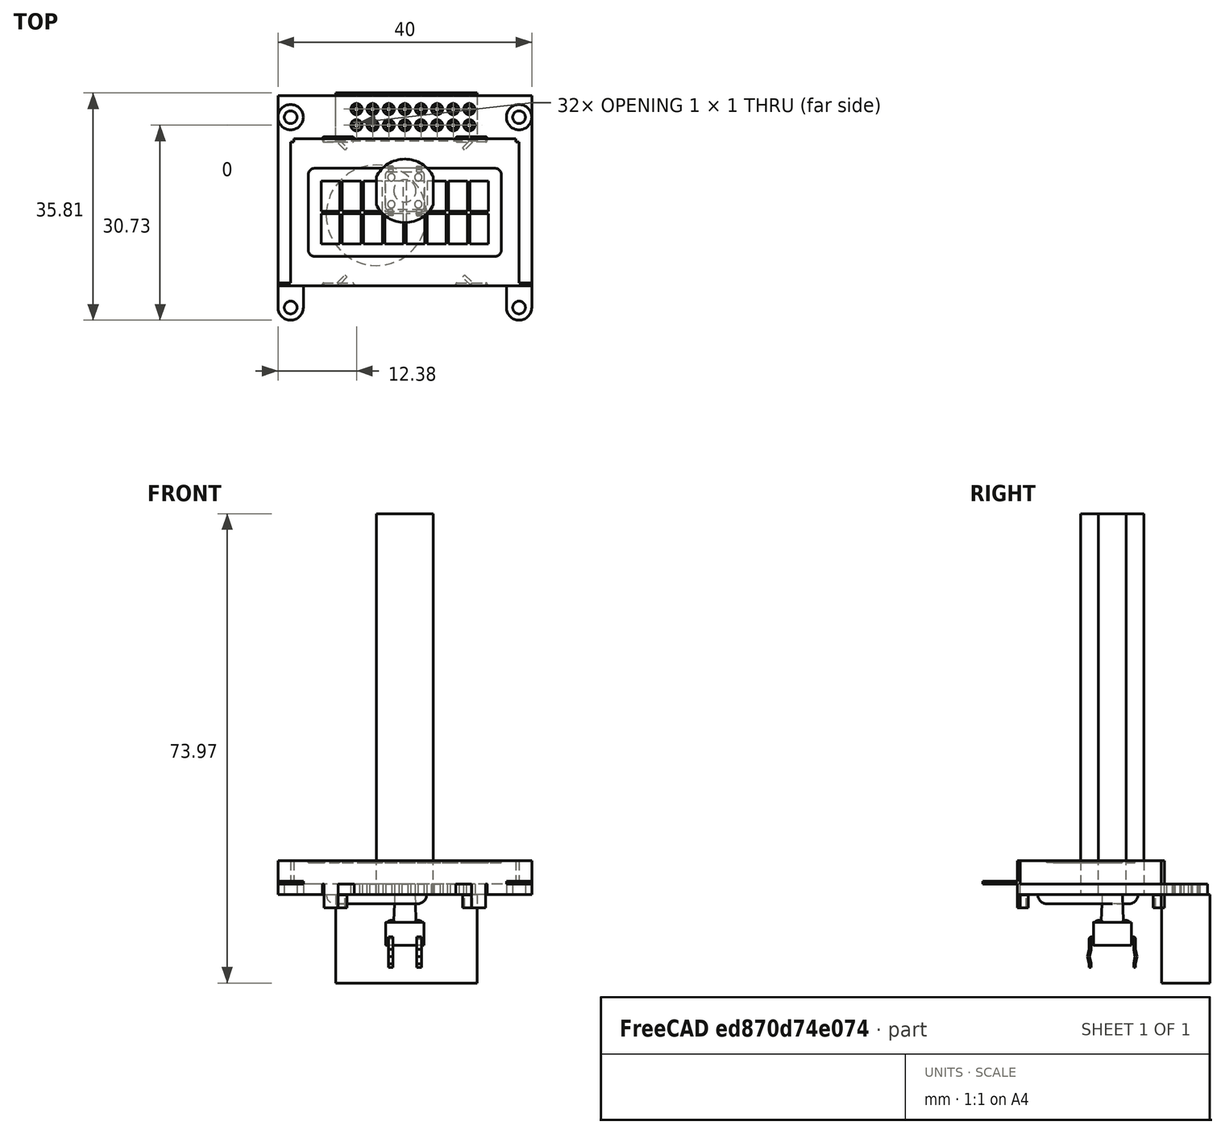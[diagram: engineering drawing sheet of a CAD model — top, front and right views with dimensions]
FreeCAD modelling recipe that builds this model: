
FCSTD DOCUMENT  (FreeCAD 1.0R39109 (Git))
Label: WwvbClockComponents
License: All rights reserved
LicenseURL: https://en.wikipedia.org/wiki/All_rights_reserved
objects: Part::Feature×20, App::Link×15, App::FeaturePython×7, Sketcher::SketchObject×2, PartDesign::Pad×2, PartDesign::SubShapeBinder×2, PartDesign::Body×2, App::Part×2, Assembly::AssemblyLink×1, Spreadsheet::Sheet×1, Assembly::JointGroup×1, Assembly::AssemblyObject×1
note: 34 computed .brp shape members not serialized (recipe doc carries the construction recipe); baked Part::Feature solids carry a one-line shape summary decoded from their .brp
EXTERNAL_REF file=ClockRaytrace.FCStd obj=Spreadsheet
EXTERNAL_REF file=ClockRaytrace.FCStd obj=Part006
EXTERNAL_REF file=PCB/PCB.FCStd obj=Assembly
EXTERNAL_REF file=PCB/PCB.FCStd obj=Teensy
EXTERNAL_REF file=PCB/PCB.FCStd obj=Part001
EXTERNAL_REF file=PCB/PCB.FCStd obj=Part003
EXTERNAL_REF file=PCB/PCB.FCStd obj=Body004
EXTERNAL_REF file=PCB/PCB.FCStd obj=Body
EXTERNAL_REF file=PCB/PCB.FCStd obj=PSK_receiver
EXTERNAL_REF file=PCB/PCB.FCStd obj=Teensy_header
EXTERNAL_REF file=PCB/PCB.FCStd obj=Teensy_header001
EXTERNAL_REF file=ClockRaytrace.FCStd obj=Body001

FEATURE [App::Link] Link002  label="Spreadsheet"
  LinkedObject = -> <external ClockRaytrace.FCStd>#Spreadsheet
FEATURE [Part::Feature] Part__Feature  label="NHD-0208AZ-RN"
  shape: bbox 4 x 4 x 1.602 mm, 6 faces (baked)
FEATURE [Part::Feature] Part__Feature001  label="NHD-0208AZ-RN001"
  shape: bbox 4 x 4 x 1.602 mm, 6 faces (baked)
FEATURE [Part::Feature] Part__Feature002  label="NHD-0208AZ-RN002"
  shape: bbox 1.8 x 1.8 x 1.602 mm, 6 faces (baked)
FEATURE [Part::Feature] Part__Feature003  label="NHD-0208AZ-RN003"
  shape: bbox 1.8 x 1.8 x 1.602 mm, 6 faces (baked)
FEATURE [Part::Feature] Part__Feature004  label="NHD-0208AZ-RN004"
  shape: bbox 1.8 x 1.8 x 1.602 mm, 6 faces (baked)
FEATURE [Part::Feature] Part__Feature005  label="NHD-0208AZ-RN005"
  shape: bbox 1.8 x 1.8 x 1.602 mm, 6 faces (baked)
FEATURE [Part::Feature] Part__Feature006  label="NHD-0208AZ-RN006"
  shape: bbox 1.8 x 1.8 x 1.602 mm, 6 faces (baked)
FEATURE [Part::Feature] Part__Feature007  label="NHD-0208AZ-RN007"
  shape: bbox 1.8 x 1.8 x 1.602 mm, 6 faces (baked)
FEATURE [Part::Feature] Part__Feature008  label="NHD-0208AZ-RN008"
  shape: bbox 1.8 x 1.8 x 1.602 mm, 6 faces (baked)
FEATURE [Part::Feature] Part__Feature009  label="NHD-0208AZ-RN009"
  shape: bbox 1.8 x 1.8 x 1.602 mm, 6 faces (baked)
FEATURE [Part::Feature] Part__Feature010  label="NHD-0208AZ-RN010"
  shape: bbox 1.8 x 1.8 x 1.602 mm, 6 faces (baked)
FEATURE [Part::Feature] Part__Feature011  label="NHD-0208AZ-RN011"
  shape: bbox 1.8 x 1.8 x 1.602 mm, 6 faces (baked)
FEATURE [Part::Feature] Part__Feature012  label="NHD-0208AZ-RN012"
  shape: bbox 1.8 x 1.8 x 1.602 mm, 6 faces (baked)
FEATURE [Part::Feature] Part__Feature013  label="NHD-0208AZ-RN013"
  shape: bbox 1.8 x 1.8 x 1.602 mm, 6 faces (baked)
FEATURE [Part::Feature] Part__Feature014  label="NHD-0208AZ-RN014"
  shape: bbox 1.8 x 1.8 x 1.602 mm, 6 faces (baked)
FEATURE [Part::Feature] Part__Feature015  label="NHD-0208AZ-RN015"
  shape: bbox 1.8 x 1.8 x 1.602 mm, 6 faces (baked)
FEATURE [Part::Feature] Part__Feature016  label="NHD-0208AZ-RN016"
  shape: bbox 1.8 x 1.8 x 1.602 mm, 6 faces (baked)
FEATURE [Part::Feature] Part__Feature017  label="NHD-0208AZ-RN017"
  shape: bbox 1.8 x 1.8 x 1.602 mm, 6 faces (baked)
FEATURE [Part::Feature] Part__Feature018  label="NHD-0208AZ-RN018"
  shape: bbox 40 x 35.4 x 7.4 mm, 222 faces (baked)
FEATURE [Part::Feature] Part__Feature019  label="Switch 1"
  shape: bbox 5.99 x 7.8 x 11.51 mm, 99 faces (baked)
FEATURE [Sketcher::SketchObject] Sketch007
  ArcFitTolerance = 1e-06
  AttachmentSupport = -> [XY_Plane016]
  FullyConstrained = true
  MakeInternals = false
  MapMode = 5
  sketch-geometry (5):
    g0: ArcOfCircle CenterX=0 CenterY=0 CenterZ=0 NormalX=0 NormalY=0 NormalZ=1 AngleXU=0 Radius=5 StartAngle=0.451027 EndAngle=2.69057
    g1: LineSegment StartX=4.5 StartY=-2.17945 StartZ=0 EndX=4.5 EndY=2.17945 EndZ=0
    g2: LineSegment StartX=-4.5 StartY=2.17945 StartZ=0 EndX=-4.5 EndY=-2.17945 EndZ=0
    g3: GeomPoint [constr] X=0 Y=0 Z=0
    g4: ArcOfCircle CenterX=0 CenterY=0 CenterZ=0 NormalX=0 NormalY=0 NormalZ=1 AngleXU=0 Radius=5 StartAngle=3.59262 EndAngle=5.83216
  constraints (14):
    c: Coincident(g0,g-1)
    c: Diameter(g0) = 10
    c: Vertical(g1)
    c: Vertical(g2)
    c: Coincident(g3,g0)
    c: Coincident(g0,g1)
    c: Coincident(g1,g4)
    c: PointOnObject(g2,g4)
    c: Equal(g0,g4)
    c: PointOnObject(g4,g2)
    c: Coincident(g0,g4)
    c: Coincident(g2,g0)
    c: DistanceX(g0,g0) = 9
    c: Equal(g2,g1)
FEATURE [PartDesign::Pad] Pad005
  Direction = (0,0,1)
  Length = 60
  Length2 = 10
  Profile = -> Sketch007
  ReferenceAxis = -> Sketch007 [N_Axis]
  Refine = true
  Suppressed = false
  Type = 0
FEATURE [App::Link] LED
  LinkPlacement = pos=(15,0,-5.08) rot=(0,0,1;1.5708rad)
  LinkedObject = -> <external ClockRaytrace.FCStd>#Part006
  Placement = pos=(15,0,-5.08) rot=(0,0,1;1.5708rad)
  expr: .Placement.Base.z = -<<Spreadsheet>>.Base_LED_Package_Height
  expr: .Placement.Rotation.Yaw = <<Spreadsheet>>.Base_LED_yaw_angle
FEATURE [App::FeaturePython] GroundedJoint  label="LED002"  # Assembly grounded joint (typed FeaturePython)
  ObjectToGround = -> LED
  Placement = pos=(15,0,-5.08) rot=(0,0,1;1.5708rad)
FEATURE [App::Link] Teensy  label="Teensy001"
  LinkPlacement = pos=(22.0851,8.84038,14.921) rot=(0,0,1;4.71239rad)
  LinkedObject = -> <external PCB/PCB.FCStd>#Teensy
  Placement = pos=(22.0851,8.84038,14.921) rot=(0,0,1;4.71239rad)
FEATURE [App::Link] Part001  label="PJ-202A"
  LinkPlacement = pos=(35.1848,67.2072,8.325) rot=(0.57735,0.57735,0.57735;2.0944rad)
  LinkedObject = -> <external PCB/PCB.FCStd>#Part001
  Placement = pos=(35.1848,67.2072,8.325) rot=(0.57735,0.57735,0.57735;2.0944rad)
FEATURE [App::Link] Part003  label="connect to LCD"
  LinkPlacement = pos=(38.0997,17.4048,-0.214) rot=(0.57735,0.57735,-0.57735;4.18879rad)
  LinkedObject = -> <external PCB/PCB.FCStd>#Part003
  Placement = pos=(38.0997,17.4048,-0.214) rot=(0.57735,0.57735,-0.57735;4.18879rad)
FEATURE [App::Link] Body004  label="PCB"
  LinkedObject = -> <external PCB/PCB.FCStd>#Body004
FEATURE [App::Link] LED001
  LinkPlacement = pos=(25.16,1.4e-15,-5.08) rot=(0,0,1;1.5708rad)
  LinkedObject = -> <external ClockRaytrace.FCStd>#Part006
  Placement = pos=(25.16,1.4e-15,-5.08) rot=(0,0,1;1.5708rad)
FEATURE [App::FeaturePython] Joint001  label="Fixed"  # Assembly joint (typed FeaturePython)
  Activated = true
  AngleMax = 0
  AngleMin = 0
  Detach1 = false
  Detach2 = false
  Distance = 0
  Distance2 = 0
  EnableAngleMax = false
  EnableAngleMin = false
  EnableLengthMax = false
  EnableLengthMin = false
  JointType = 0 (Fixed)
  LengthMax = 0
  LengthMin = 0
  Offset1 = pos=(0,0,0) rot=(0,0,1;3.14159rad)
  Placement1 = pos=(2e-16,5.08,2.54) rot=(0,0.707107,0.707107;3.14159rad)
  Placement2 = pos=(-2e-16,-5.08,2.54) rot=(0,-0.707107,0.707107;3.14159rad)
  Reference1 = -> Assembly [LED001.Body.Face2,LED001.Body.Face2]
  Reference2 = -> Assembly [LED.Body.Face3,LED.Body.Face3]
FEATURE [App::FeaturePython] GroundedJoint002  label="2nd LED"  # Assembly grounded joint (typed FeaturePython)
  ObjectToGround = -> LED001
  Placement = pos=(25.16,1.4e-15,-5.08) rot=(0,0,1;1.5708rad)
FEATURE [App::Link] Body008  label="Keystone 103"
  LinkPlacement = pos=(26.67,34.635,-2.52) rot=(0.707107,0.707107,0;3.14159rad)
  LinkedObject = -> <external PCB/PCB.FCStd>#Body
  Placement = pos=(26.67,34.635,-2.52) rot=(0.707107,0.707107,0;3.14159rad)
FEATURE [App::Link] PSK_receiver  label="PSK receiver"
  LinkPlacement = pos=(-36.1561,29.1871,-3.151) rot=(0,0,1;0rad)
  LinkedObject = -> <external PCB/PCB.FCStd>#PSK_receiver
  Placement = pos=(-36.1561,29.1871,-3.151) rot=(0,0,1;0rad)
FEATURE [App::FeaturePython] Joint  label="Revolute"  # Assembly joint (typed FeaturePython)
  Activated = true
  AngleMax = 0
  AngleMin = 0
  Detach1 = false
  Detach2 = false
  Distance = 0
  Distance2 = 0
  EnableAngleMax = false
  EnableAngleMin = false
  EnableLengthMax = false
  EnableLengthMin = false
  JointType = 1 (Revolute)
  LengthMax = 0
  LengthMin = 0
  Offset1 = pos=(0,0,-2.413) rot=(0,0,1;3.14159rad)
  Placement1 = pos=(-6.35,-3.81,-1.905) rot=(0,-1,0;3.14159rad)
  Placement2 = pos=(23.6297,62.23,0) rot=(0,0,1;0rad)
  Reference1 = -> Assembly [LED001.Body.Edge18,LED001.Body.Edge18]
  Reference2 = -> Assembly [Assembly001.Body004.HoleSketch.Edge10,Assembly001.Body004.HoleSketch.Edge10]
FEATURE [PartDesign::SubShapeBinder] Binder
  BindCopyOnChange = 0
  BindMode = 0
  ClaimChildren = false
  Context = -> Part [Body007.Binder.]
  Fuse = false
  MakeFace = true
  OffsetFill = false
  OffsetIntersection = false
  OffsetJoinType = 0
  OffsetOpenResult = false
  PartialLoad = false
  Refine = true
  Relative = true
  Support = -> [Assembly[Assembly001.Body008.Pad001.Face1]]
  _Version = 2
FEATURE [PartDesign::Body] Body007
  AllowCompound = false
  Group = -> [Sketch007,Pad005,Binder]
  Origin = -> Origin016
  Tip = -> Pad005
FEATURE [App::Part] Part  label="Antenna"
  Group = -> [Body007]
  Origin = -> Origin015
  Placement = pos=(-31.75,-2.54,-22.86) rot=(0.57735,0.57735,0.57735;2.0944rad)
FEATURE [App::Link] LCD_panel  label="LCD panel001"
  LinkPlacement = pos=(-29.21,-3.556,33.02) rot=(0.497543,-0.497543,-0.710565;1.90603rad)
  LinkedObject = -> NHD_0208AZ_RN
  Placement = pos=(-29.21,-3.556,33.02) rot=(0.497543,-0.497543,-0.710565;1.90603rad)
FEATURE [App::Link] Teensy_header  label="Teensy header"
  LinkPlacement = pos=(62.8687,-3.88149,1.778) rot=(0,0,1;1.5708rad)
  LinkedObject = -> <external PCB/PCB.FCStd>#Teensy_header
  Placement = pos=(62.8687,-3.88149,1.778) rot=(0,0,1;1.5708rad)
FEATURE [App::Link] Teensy_header001  label="Teensy header001"
  LinkPlacement = pos=(62.8687,11.3585,1.778) rot=(0,0,1;1.5708rad)
  LinkedObject = -> <external PCB/PCB.FCStd>#Teensy_header001
  Placement = pos=(62.8687,11.3585,1.778) rot=(0,0,1;1.5708rad)
FEATURE [Assembly::AssemblyLink] Assembly001  label="PCB001"
  Group = -> [Teensy,Part001,Part003,Body004,Body008,PSK_receiver,Teensy_header,Teensy_header001]
  LinkedObject = -> <external PCB/PCB.FCStd>#Assembly
  Origin = -> Origin018
  Placement = pos=(-33.26,17.2797,-6.985) rot=(0,0,-1;1.5708rad)
  Rigid = true
FEATURE [App::FeaturePython] GroundedJoint003  label="LCD"  # Assembly grounded joint (typed FeaturePython)
  ObjectToGround = -> LCD_panel
  Placement = pos=(-29.21,-3.556,33.02) rot=(0.497543,-0.497543,-0.710565;1.90603rad)
FEATURE [App::Link] _8mm50FLLens  label="38mm50FLLens"
  LinkPlacement = pos=(5,0,51) rot=(0,0,1;0rad)
  LinkedObject = -> <external ClockRaytrace.FCStd>#Body001
  Placement = pos=(5,0,51) rot=(0,0,1;0rad)
  expr: .Placement.Base.x = 15 mm - <<Spreadsheet>>.Base_Lens_X_offset
  expr: .Placement.Base.z = <<Spreadsheet>>.Base_LensToLED
FEATURE [PartDesign::SubShapeBinder] Binder001
  BindCopyOnChange = 0
  BindMode = 0
  ClaimChildren = false
  Context = -> NHD_0208AZ_RN [Body.Binder001.]
  Fuse = false
  MakeFace = true
  OffsetFill = false
  OffsetIntersection = false
  OffsetJoinType = 0
  OffsetOpenResult = false
  PartialLoad = false
  Refine = true
  Relative = true
  Support = -> [Part__Feature018]
  _Version = 2
FEATURE [Sketcher::SketchObject] Sketch
  ArcFitTolerance = 1e-06
  AttachmentSupport = -> [Binder001]
  ExternalGeometry = -> [Binder001]
  FullyConstrained = true
  MakeInternals = false
  MapMode = 5
  Placement = pos=(0,0,0) rot=(1,0,0;3.14159rad)
  sketch-geometry (4):
    g0: LineSegment StartX=-10.922 StartY=-7.79 StartZ=0 EndX=-10.922 EndY=-15.41 EndZ=0
    g1: LineSegment StartX=-10.922 StartY=-15.41 StartZ=0 EndX=11.422 EndY=-15.41 EndZ=0
    g2: LineSegment StartX=11.422 StartY=-15.41 StartZ=0 EndX=11.422 EndY=-7.79 EndZ=0
    g3: LineSegment StartX=11.422 StartY=-7.79 StartZ=0 EndX=-10.922 EndY=-7.79 EndZ=0
  constraints (12):
    c: Coincident(g0,g1)
    c: Coincident(g1,g2)
    c: Coincident(g2,g3)
    c: Coincident(g3,g0)
    c: Vertical(g0)
    c: Vertical(g2)
    c: Horizontal(g1)
    c: Horizontal(g3)
    c: DistanceX(g0,g-4) = 3.302
    c: DistanceX(g-3,g2) = 3.302
    c: DistanceY(g0,g-4) = 2.54
    c: DistanceY(g-3,g2) = 2.54
FEATURE [PartDesign::Pad] Pad
  Direction = (0,0,-1)
  Length = 13.97
  Length2 = 10
  Profile = -> Sketch
  ReferenceAxis = -> Sketch [N_Axis]
  Refine = true
  Suppressed = false
  Type = 0
FEATURE [PartDesign::Body] Body
  AllowCompound = false
  Group = -> [Binder001,Sketch,Pad]
  Origin = -> Origin019
  Tip = -> Pad
FEATURE [App::Part] NHD_0208AZ_RN  label="LCD panel"
  Group = -> [Part__Feature,Part__Feature001,Part__Feature002,Part__Feature003,Part__Feature004,Part__Feature005,Part__Feature006,Part__Feature007,Part__Feature008,Part__Feature009,Part__Feature010,Part__Feature011,Part__Feature012,Part__Feature013,Part__Feature014,Part__Feature015,Part__Feature016,Part__Feature017,Part__Feature018,Body]
  Origin = -> Origin
FEATURE [App::Link] Switch_1  label="Switch 002"
  LinkPlacement = pos=(-17.5,-20,53.3) rot=(0,0,1;0rad)
  LinkedObject = -> Part__Feature019
  Placement = pos=(-17.5,-20,53.3) rot=(0,0,1;0rad)
FEATURE [App::Link] Switch_002  label="Switch 003"
  LinkPlacement = pos=(-17.5,13.61,53.3) rot=(0,0,1;0rad)
  LinkedObject = -> Part__Feature019
  Placement = pos=(-17.5,13.61,53.3) rot=(0,0,1;0rad)
FEATURE [Spreadsheet::Sheet] Spreadsheet  label="Spreadsheet001"
  Base_Antenna_X_Offset = 0
  Base_Antenna_Y_Offset = 2.54
  Base_Antenna_Z_Offset = -25.4
FEATURE [App::FeaturePython] GroundedJoint005  # Assembly grounded joint (typed FeaturePython)
  ObjectToGround = -> Switch_002
  Placement = pos=(-17.5,13.61,53.3) rot=(0,0,1;0rad)
FEATURE [App::FeaturePython] GroundedJoint006  # Assembly grounded joint (typed FeaturePython)
  ObjectToGround = -> Switch_1
  Placement = pos=(-17.5,-20,53.3) rot=(0,0,1;0rad)
FEATURE [Assembly::JointGroup] Joints
  Group = -> [GroundedJoint,Joint001,GroundedJoint002,Joint,GroundedJoint003,GroundedJoint005,GroundedJoint006]
FEATURE [Assembly::AssemblyObject] Assembly
  Group = -> [Joints,LED,GroundedJoint,Assembly001,LED001,Joint001,GroundedJoint002,Joint,LCD_panel,GroundedJoint003,_8mm50FLLens,Switch_1,Switch_002,GroundedJoint005,GroundedJoint006]
  Origin = -> Origin017
  Type = Assembly

RESOLVED EXTERNAL PARTS (link-assembly join: the EXTERNAL_REF files above that resolve inside this repo's crawl, each included once):
---- part ClockRaytrace.FCStd = doc fcstd_c784e775d372 ----
FCSTD DOCUMENT  (FreeCAD 1.0R39109 (Git))
Label: ClockRaytrace
License: All rights reserved
LicenseURL: https://en.wikipedia.org/wiki/All_rights_reserved
objects: Part::FeaturePython×11, Sketcher::SketchObject×5, PartDesign::Body×4, PartDesign::Pad×4, App::Link×2, App::DocumentObjectGroup×2, PartDesign::Revolution×1, PartDesign::ShapeBinder×1, Spreadsheet::Sheet×1, App::Part×1
note: 41 computed .brp shape members not serialized (recipe doc carries the construction recipe); baked Part::Feature solids carry a one-line shape summary decoded from their .brp

FEATURE [Sketcher::SketchObject] Sketch001
  ArcFitTolerance = 1e-06
  AttachmentSupport = -> [XZ_Plane003]
  FullyConstrained = true
  MakeInternals = false
  MapMode = 5
  Placement = pos=(0,0,0) rot=(1,0,0;1.5708rad)
  sketch-geometry (7):
    g0: LineSegment StartX=0 StartY=3.99545 StartZ=0 EndX=0 EndY=-3.99545 EndZ=0
    g1: LineSegment [constr] StartX=0 StartY=0 StartZ=0 EndX=19 EndY=0 EndZ=0
    g2: LineSegment StartX=19 StartY=0.4 StartZ=0 EndX=19 EndY=-0.4 EndZ=0
    g3: Circle [constr] CenterX=0 CenterY=-48.0045 CenterZ=0 NormalX=0 NormalY=0 NormalZ=1 AngleXU=0 Radius=52
    g4: ArcOfCircle CenterX=1.31e-14 CenterY=-48.0045 CenterZ=0 NormalX=0 NormalY=0 NormalZ=1 AngleXU=0 Radius=52 StartAngle=1.19675 EndAngle=1.5708
    g5: Circle [constr] CenterX=0 CenterY=48.0045 CenterZ=0 NormalX=0 NormalY=0 NormalZ=1 AngleXU=0 Radius=52
    g6: ArcOfCircle CenterX=4.1e-15 CenterY=48.0045 CenterZ=0 NormalX=0 NormalY=0 NormalZ=1 AngleXU=0 Radius=52 StartAngle=4.71239 EndAngle=5.08643
  constraints (21):
    c: Vertical(g0)
    c: Symmetric(g0,g0,g-1)
    c: Coincident(g1,g-1)
    c: PointOnObject(g1,g-1)
    c: DistanceX(g1,g1) = 19
    c: Vertical(g2)
    c: Symmetric(g2,g2,g1)
    c: Radius(g3) = 52
    c: Vertical(g3,g0)
    c: PointOnObject(g2,g3)
    c: PointOnObject(g0,g3)
    c: Coincident(g4,g0)
    c: Coincident(g4,g2)
    c: Vertical(g5,g0)
    c: Equal(g5,g3)
    c: PointOnObject(g2,g5)
    c: Coincident(g6,g2)
    c: Coincident(g6,g0)
    c: Equal(g4,g3)
    c: Equal(g5,g6)
    c: DistanceY(g2,g2) = 0.8
FEATURE [PartDesign::Revolution] Revolution001
  Angle = 360
  Angle2 = 60
  Axis = (0,2e-16,1)
  Base = (0,0,0)
  Placement = pos=(0,0,0) rot=(1,0,0;1.5708rad)
  Profile = -> Sketch001
  ReferenceAxis = -> Sketch001 [V_Axis]
  Refine = true
  Reversed = true
  Suppressed = false
  Type = 0
FEATURE [PartDesign::Body] Body001  label="38mm50FLLens"
  AllowCompound = false
  Group = -> [Sketch001,Revolution001]
  Origin = -> Origin003
  Tip = -> Revolution001
FEATURE [Part::FeaturePython] Beam  # WARN: FeaturePython — macro-defined, semantics opaque (R4)
  BeamDistance = 0.1
  BeamNrColumns = 10
  BeamNrRows = 10
  ConeAngle = 90
  HideFirstPart = false
  MaxNrReflections = 200
  MaxRayLength = 1000000
  Order = 0
  Placement = pos=(1.855,-7.73,0) rot=(-1,0,0;0.05236rad)
  Power = true
  Spherical = true
  Wavelength = 580
  expr: .Placement.Base.x = Spreadsheet.Base_LED_Height / 2 + Spreadsheet.Base_LED_X_offset
  expr: .Placement.Base.y = -Spreadsheet.Base_LED_Width / 2
  expr: BeamNrColumns = Spreadsheet.Base_Source_Columns
  expr: BeamNrRows = Spreadsheet.Base_Source_Rows
  expr: ConeAngle = Spreadsheet.Base_SourceConeAngle
FEATURE [Part::FeaturePython] Beam001  # WARN: FeaturePython — macro-defined, semantics opaque (R4)
  BeamDistance = 0.1
  BeamNrColumns = 10
  BeamNrRows = 10
  ConeAngle = 90
  HideFirstPart = false
  MaxNrReflections = 200
  MaxRayLength = 1000000
  Order = 0
  Placement = pos=(-1.855,0,0) rot=(0,1,0;0rad)
  Power = true
  Spherical = true
  Wavelength = 580
  expr: .Placement.Base.x = -Spreadsheet.Base_LED_Height / 2 + Spreadsheet.Base_LED_X_offset
  expr: BeamNrColumns = Spreadsheet.Base_Source_Columns
  expr: BeamNrRows = Spreadsheet.Base_Source_Rows
  expr: ConeAngle = Spreadsheet.Base_SourceConeAngle
FEATURE [Part::FeaturePython] Beam002  # WARN: FeaturePython — macro-defined, semantics opaque (R4)
  BeamDistance = 1
  BeamNrColumns = 40
  BeamNrRows = 1
  ConeAngle = 360
  HideFirstPart = false
  MaxNrReflections = 200
  MaxRayLength = 1000000
  Order = 0
  Placement = pos=(20,0,0) rot=(0.57735,-0.57735,0.57735;2.0944rad)
  Power = true
  Spherical = false
  Wavelength = 580
FEATURE [Part::FeaturePython] Beam003  # WARN: FeaturePython — macro-defined, semantics opaque (R4)
  BeamDistance = 0.1
  BeamNrColumns = 10
  BeamNrRows = 10
  ConeAngle = 90
  HideFirstPart = false
  MaxNrReflections = 200
  MaxRayLength = 1000000
  Order = 0
  Placement = pos=(1.855,7.73,0) rot=(1,0,0;0.069813rad)
  Power = true
  Spherical = true
  Wavelength = 580
  expr: .Placement.Base.x = Spreadsheet.Base_LED_Height / 2 + Spreadsheet.Base_LED_X_offset
  expr: .Placement.Base.y = Spreadsheet.Base_LED_Width / 2
  expr: BeamNrColumns = Spreadsheet.Base_Source_Columns
  expr: BeamNrRows = Spreadsheet.Base_Source_Rows
  expr: ConeAngle = Spreadsheet.Base_SourceConeAngle
FEATURE [PartDesign::ShapeBinder] CopyPad004
  TraceSupport = false
FEATURE [Sketcher::SketchObject] Sketch
  ArcFitTolerance = 1e-06
  AttachmentSupport = -> [CopyPad004]
  FullyConstrained = true
  MakeInternals = false
  MapMode = 5
  Placement = pos=(0,0,0) rot=(1,0,0;3.14159rad)
  sketch-geometry (5):
    g0: LineSegment StartX=8.89 StartY=-5.08 StartZ=0 EndX=8.89 EndY=5.08 EndZ=0
    g1: LineSegment StartX=8.89 StartY=5.08 StartZ=0 EndX=-8.89 EndY=5.08 EndZ=0
    g2: LineSegment StartX=-8.89 StartY=5.08 StartZ=0 EndX=-8.89 EndY=-5.08 EndZ=0
    g3: LineSegment StartX=-8.89 StartY=-5.08 StartZ=0 EndX=8.89 EndY=-5.08 EndZ=0
    g4: GeomPoint [constr] X=0 Y=0 Z=0
  constraints (12):
    c: Coincident(g0,g1)
    c: Coincident(g1,g2)
    c: Coincident(g2,g3)
    c: Coincident(g3,g0)
    c: Vertical(g0)
    c: Vertical(g2)
    c: Horizontal(g1)
    c: Horizontal(g3)
    c: Symmetric(g2,g0,g4)
    c: Coincident(g4,g-1)
    c: DistanceY(g0,g0) = 10.16
    c: DistanceX(g1,g1) = 17.78
FEATURE [PartDesign::Pad] Pad
  Direction = (0,0,-1)
  Length = 5.08
  Length2 = 10
  Profile = -> Sketch
  ReferenceAxis = -> Sketch [N_Axis]
  Refine = true
  Reversed = true
  Suppressed = false
  Type = 0
FEATURE [Sketcher::SketchObject] Sketch011
  ArcFitTolerance = 1e-06
  AttachmentSupport = -> [XY_Plane019]
  FullyConstrained = false
  MakeInternals = false
  MapMode = 5
  sketch-geometry (3):
    g0: Circle CenterX=0 CenterY=0 CenterZ=0 NormalX=0 NormalY=0 NormalZ=1 AngleXU=0 Radius=20
    g1: Circle CenterX=0 CenterY=0 CenterZ=0 NormalX=0 NormalY=0 NormalZ=1 AngleXU=0 Radius=21.5748
    g2: LineSegment [constr] StartX=0.010426 StartY=20 StartZ=0 EndX=0.010426 EndY=21.5748 EndZ=0
  constraints (7):
    c: Coincident(g0,g-1)
    c: Coincident(g1,g0)
    c: Diameter(g0) = 40
    c: PointOnObject(g2,g0)
    c: PointOnObject(g2,g1)
    c: Vertical(g2)
    c: DistanceY(g2,g2) = 1.5748
FEATURE [PartDesign::Pad] Pad006
  Direction = (0,0,1)
  Length = 48
  Length2 = 10
  Profile = -> Sketch011
  ReferenceAxis = -> Sketch011 [N_Axis]
  Refine = true
  Reversed = true
  Suppressed = false
  Type = 0
  expr: Length = Spreadsheet.Base_LensToLED - 3 mm
FEATURE [PartDesign::Body] Body010  label="baffle"
  AllowCompound = false
  Group = -> [Sketch011,Pad006]
  Origin = -> Origin019
  Placement = pos=(-7.46,0,48) rot=(0,-1,0;0.314159rad)
  Tip = -> Pad006
  expr: .Placement.Base.x = 2.54 mm - Spreadsheet.Base_Lens_X_offset
  expr: .Placement.Base.z = Spreadsheet.Base_LensToLED - 3 mm
FEATURE [Part::FeaturePython] Absorber001  # WARN: FeaturePython — macro-defined, semantics opaque (R4)
  Base = -> [Body010]
  OpticalType = 1
  Transparency = 0
  collectStatistics = false
FEATURE [Spreadsheet::Sheet] Spreadsheet
  Base_Ceiling_Target_Height = 101.6
  Base_Ceiling_Target_Width = 254
  Base_DeviceTilt = 0
  Base_LED_Height = 3.71
  Base_LED_Package_Height = 5.08
  Base_LED_Width = 15.46
  Base_LED_X_offset = 0
  Base_LED_Y_offset = 0
  Base_LED_yaw_angle = 90
  Base_LEDtoCeiling = 1397
  Base_LensToLED = 51
  Base_Lens_X_offset = 10
  Base_SourceConeAngle = 90
  Base_Source_Columns = 10
  Base_Source_Rows = 10
  Base_XOffset_LED_to_Ceiling = -248.158
FEATURE [Part::FeaturePython] Beam004  # WARN: FeaturePython — macro-defined, semantics opaque (R4)
  BeamDistance = 0.1
  BeamNrColumns = 10
  BeamNrRows = 10
  ConeAngle = 90
  HideFirstPart = false
  MaxNrReflections = 200
  MaxRayLength = 1000000
  Order = 0
  Placement = pos=(-1.855,-7.73,0) rot=(-1,0,0;0.05236rad)
  Power = true
  Spherical = true
  Wavelength = 580
  expr: .Placement.Base.x = -Spreadsheet.Base_LED_Height / 2 + Spreadsheet.Base_LED_X_offset
  expr: .Placement.Base.y = -Spreadsheet.Base_LED_Width / 2
  expr: BeamNrColumns = Spreadsheet.Base_Source_Columns
  expr: BeamNrRows = Spreadsheet.Base_Source_Rows
  expr: ConeAngle = Spreadsheet.Base_SourceConeAngle
FEATURE [Part::FeaturePython] Beam005  # WARN: FeaturePython — macro-defined, semantics opaque (R4)
  BeamDistance = 0.1
  BeamNrColumns = 10
  BeamNrRows = 10
  ConeAngle = 90
  HideFirstPart = false
  MaxNrReflections = 200
  MaxRayLength = 1000000
  Order = 0
  Placement = pos=(1.855,0,0) rot=(-1,0,0;0.05236rad)
  Power = true
  Spherical = true
  Wavelength = 580
  expr: .Placement.Base.x = Spreadsheet.Base_LED_Height / 2 + <<Spreadsheet>>.Base_LED_X_offset
  expr: .Placement.Base.y = 0 in
  expr: BeamNrColumns = Spreadsheet.Base_Source_Columns
  expr: BeamNrRows = Spreadsheet.Base_Source_Rows
  expr: ConeAngle = Spreadsheet.Base_SourceConeAngle
FEATURE [Part::FeaturePython] Beam006  # WARN: FeaturePython — macro-defined, semantics opaque (R4)
  BeamDistance = 0.1
  BeamNrColumns = 10
  BeamNrRows = 10
  ConeAngle = 90
  HideFirstPart = false
  MaxNrReflections = 200
  MaxRayLength = 1000000
  Order = 0
  Placement = pos=(-1.855,7.73,0) rot=(1,0,0;0.069813rad)
  Power = true
  Spherical = true
  Wavelength = 580
  expr: .Placement.Base.x = -Spreadsheet.Base_LED_Height / 2 + Spreadsheet.Base_LED_X_offset
  expr: .Placement.Base.y = Spreadsheet.Base_LED_Width / 2
  expr: BeamNrColumns = Spreadsheet.Base_Source_Columns
  expr: BeamNrRows = Spreadsheet.Base_Source_Rows
  expr: ConeAngle = Spreadsheet.Base_SourceConeAngle
FEATURE [Sketcher::SketchObject] Sketch012
  ArcFitTolerance = 1e-06
  AttachmentSupport = -> [XZ_Plane022]
  FullyConstrained = true
  MakeInternals = false
  MapMode = 5
  Placement = pos=(0,0,0) rot=(0,0.707107,0.707107;3.14159rad)
  sketch-geometry (6):
    g0: LineSegment StartX=-76.2 StartY=0 StartZ=0 EndX=-76.2 EndY=1390.42 EndZ=0
    g1: LineSegment StartX=-76.2 StartY=1390.42 StartZ=0 EndX=1751.03 EndY=1390.42 EndZ=0
    g2: LineSegment StartX=1751.03 StartY=1390.42 StartZ=0 EndX=1751.03 EndY=1391.99 EndZ=0
    g3: LineSegment StartX=1751.03 StartY=1391.99 StartZ=0 EndX=-77.7748 EndY=1391.99 EndZ=0
    g4: LineSegment StartX=-77.7748 StartY=1391.99 StartZ=0 EndX=-77.7748 EndY=0 EndZ=0
    g5: LineSegment StartX=-77.7748 StartY=0 StartZ=0 EndX=-76.2 EndY=0 EndZ=0
  constraints (18):
    c: Vertical(g0)
    c: Horizontal(g1)
    c: Coincident(g2,g1)
    c: Vertical(g2)
    c: Horizontal(g3)
    c: PointOnObject(g4,g-1)
    c: Vertical(g4)
    c: Coincident(g5,g0)
    c: DistanceY(g2,g2) = 1.5748
    c: Equal(g5,g2)
    c: Coincident(g3,g2)
    c: Coincident(g3,g4)
    c: Coincident(g1,g0)
    c: Coincident(g5,g4)
    c: DistanceX(g0,g-1) = 76.2
    c: DistanceY(g4,g4) = 1391.99
    c: DistanceX(g3,g3) = 1828.8
    c: Horizontal(g0,g-1)
FEATURE [PartDesign::Pad] Pad007
  Direction = (0,1,-2e-16)
  Length = 1524
  Length2 = 10
  Midplane = true
  Placement = pos=(0,0,0) rot=(1,0,0;1.5708rad)
  Profile = -> Sketch012
  ReferenceAxis = -> Sketch012 [N_Axis]
  Refine = true
  Suppressed = false
  Type = 0
FEATURE [PartDesign::Body] Body011  label="Wall and Ceiling"
  AllowCompound = false
  Group = -> [Sketch012,Pad007]
  Origin = -> Origin020
  Tip = -> Pad007
  expr: .Placement.Rotation.Pitch = Spreadsheet.Base_DeviceTilt
FEATURE [Part::FeaturePython] Absorber  # WARN: FeaturePython — macro-defined, semantics opaque (R4)
  Base = -> [Body011]
  OpticalType = 1
  Transparency = 0
  collectStatistics = false
FEATURE [Sketcher::SketchObject] Sketch013
  ArcFitTolerance = 1e-06
  AttachmentSupport = -> [CopyPad004]
  FullyConstrained = true
  MakeInternals = false
  MapMode = 5
  Placement = pos=(0,0,0) rot=(1,0,0;3.14159rad)
  sketch-geometry (9):
    g0: LineSegment [constr] StartX=6.35 StartY=-3.81 StartZ=0 EndX=6.35 EndY=3.81 EndZ=0
    g1: LineSegment [constr] StartX=6.35 StartY=3.81 StartZ=0 EndX=-6.35 EndY=3.81 EndZ=0
    g2: LineSegment [constr] StartX=-6.35 StartY=3.81 StartZ=0 EndX=-6.35 EndY=-3.81 EndZ=0
    g3: LineSegment [constr] StartX=-6.35 StartY=-3.81 StartZ=0 EndX=6.35 EndY=-3.81 EndZ=0
    g4: GeomPoint [constr] X=0 Y=0 Z=0
    g5: Circle CenterX=-6.35 CenterY=-3.81 CenterZ=0 NormalX=0 NormalY=0 NormalZ=1 AngleXU=0 Radius=0.3175
    g6: Circle CenterX=6.35 CenterY=-3.81 CenterZ=0 NormalX=0 NormalY=0 NormalZ=1 AngleXU=0 Radius=0.3175
    g7: Circle CenterX=6.35 CenterY=3.81 CenterZ=0 NormalX=0 NormalY=0 NormalZ=1 AngleXU=0 Radius=0.3175
    g8: Circle CenterX=-6.35 CenterY=3.81 CenterZ=0 NormalX=0 NormalY=0 NormalZ=1 AngleXU=0 Radius=0.3175
  constraints (20):
    c: Coincident(g0,g1)
    c: Coincident(g1,g2)
    c: Coincident(g2,g3)
    c: Coincident(g3,g0)
    c: Vertical(g0)
    c: Vertical(g2)
    c: Horizontal(g1)
    c: Horizontal(g3)
    c: Symmetric(g2,g0,g4)
    c: Coincident(g4,g-1)
    c: DistanceX(g1,g1) = 12.7
    c: DistanceY(g2,g2) = 7.62
    c: Coincident(g5,g2)
    c: Coincident(g6,g0)
    c: Coincident(g7,g0)
    c: Coincident(g8,g1)
    c: Equal(g5,g8)
    c: Equal(g7,g8)
    c: Equal(g6,g8)
    c: Diameter(g8) = 0.635
FEATURE [PartDesign::Pad] Pad008
  BaseFeature = -> Pad
  Direction = (0,0,-1)
  Length = 4.318
  Length2 = 10
  Profile = -> Sketch013
  ReferenceAxis = -> Sketch013 [N_Axis]
  Refine = true
  Suppressed = false
  Type = 0
FEATURE [PartDesign::Body] Body
  AllowCompound = false
  Group = -> [CopyPad004,Sketch,Pad,Sketch013,Pad008]
  Origin = -> Origin
  Tip = -> Pad008
FEATURE [App::Part] Part006  label="LED"
  Group = -> [Body]
  Origin = -> Origin013
  Placement = pos=(0,0,-5.08) rot=(0,0,1;1.5708rad)
  expr: .Placement.Base.x = Spreadsheet.Base_LED_X_offset
  expr: .Placement.Base.z = -Spreadsheet.Base_LED_Package_Height
  expr: .Placement.Rotation.Yaw = Spreadsheet.Base_LED_yaw_angle
FEATURE [App::Link] Link  label="LED001"
  LinkPlacement = pos=(10.16,0,-5.08) rot=(0,0,1;1.5708rad)
  LinkedObject = -> Part006
  Placement = pos=(10.16,0,-5.08) rot=(0,0,1;1.5708rad)
  expr: .Placement.Base.x = Spreadsheet.Base_LED_X_offset + 400 thou
FEATURE [Part::FeaturePython] Beam007  # WARN: FeaturePython — macro-defined, semantics opaque (R4)
  BeamDistance = 0.1
  BeamNrColumns = 10
  BeamNrRows = 10
  ConeAngle = 90
  HideFirstPart = false
  MaxNrReflections = 200
  MaxRayLength = 1000000
  Order = 0
  Placement = pos=(12.015,-7.62,0) rot=(0,0,1;0rad)
  Power = true
  Spherical = true
  Wavelength = 580
  expr: .Placement.Base.x = Spreadsheet.Base_LED_Height / 2 + Spreadsheet.Base_LED_X_offset + 400 thou
  expr: BeamNrColumns = Spreadsheet.Base_Source_Columns
  expr: BeamNrRows = Spreadsheet.Base_Source_Rows
  expr: ConeAngle = Spreadsheet.Base_SourceConeAngle
FEATURE [App::DocumentObjectGroup] Group001  label="LED2"
  Group = -> [Beam007]
FEATURE [App::DocumentObjectGroup] Group  label="sources"
  Group = -> [Beam,Beam001,Beam003,Beam004,Beam005,Beam006,Group001]
FEATURE [App::Link] Link001  label="38mm50FLLens001"
  LinkPlacement = pos=(-10,0,51) rot=(0,0,1;0rad)
  LinkedObject = -> Body001
  Placement = pos=(-10,0,51) rot=(0,0,1;0rad)
  expr: .Placement.Base.x = -Spreadsheet.Base_Lens_X_offset
  expr: .Placement.Base.z = Spreadsheet.Base_LensToLED
FEATURE [Part::FeaturePython] Lens  # WARN: FeaturePython — macro-defined, semantics opaque (R4)
  Base = -> [Link001]
  Material = 3
  OpticalType = 0
  RefractionIndex = 1.45873
  Sellmeier = [0.696166,0.407943,0.897479,4679.15,13512.1,97934000]
  Transparency = 100
  collectStatistics = false
